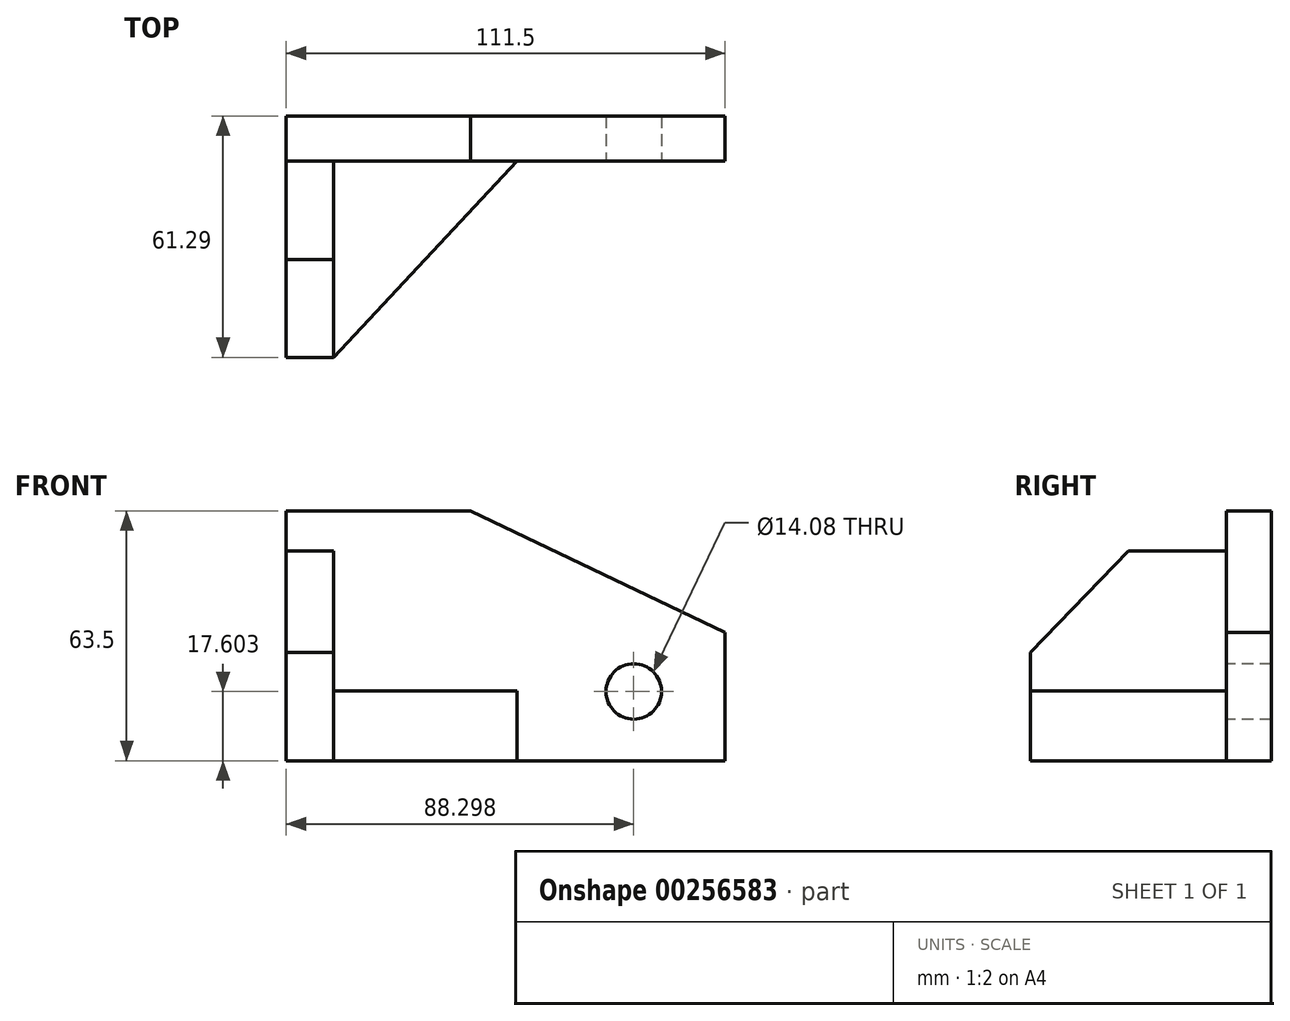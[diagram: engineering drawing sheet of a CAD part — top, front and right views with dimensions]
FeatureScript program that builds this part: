
annotation { "Feature Type Name" : "Feature", "Feature Type Description" : "" }
export const myFeature = defineFeature(function(context is Context, id is Id, definition is map)
    precondition{}
    {
        {
            var Q0;
            Q0=qCreatedBy(makeId("Top.planeOp"),FACE);
            var sketch = newSketch(context, id + "F0", { "sketchPlane" : qUnion([Q0])});
            skLineSegment(sketch, "E0.bottom", {"start": v(-51.05, 9.49) * mm, "end": v(60.45, 9.49) * mm});
            skLineSegment(sketch, "E0.top", {"start": v(-51.05, -51.8) * mm, "end": v(60.45, -51.8) * mm});
            skLineSegment(sketch, "E0.left", {"start": v(-51.05, 9.49) * mm, "end": v(-51.05, -51.8) * mm});
            skLineSegment(sketch, "E0.right", {"start": v(60.45, 9.49) * mm, "end": v(60.45, -51.8) * mm});
            skSolve(sketch);
        }
        {
            var Q0;
            Q0=makeQuery(id+"F0.imprint","IMPRINT",FACE,{"disambiguationData":[TD([[makeQuery(id+"F0.imprint","IMPRINT",EDGE,{"derivedFrom":sQuery(id+"F0.wireOp",EDGE,"E0.bottom")}),-1.0]])]});
            extrude(context, id + "F1", {"entities" : qUnion([Q0]), "depth" : 17.78 * mm});
        }
        {
            var Q0;
            Q0=makeQuery(id+"F1.opExtrude","CAP_FACE",FACE,{"disambiguationData":[OSD([sQuery(id+"F0.wireOp",EDGE,"E0.bottom"),sQuery(id+"F0.wireOp",EDGE,"E0.top"),sQuery(id+"F0.wireOp",EDGE,"E0.left"),sQuery(id+"F0.wireOp",EDGE,"E0.right")])],"isStart":false});
            var sketch = newSketch(context, id + "F2", { "sketchPlane" : qUnion([Q0])});
            skLineSegment(sketch, "E1.bottom", {"start": v(-51.05, 9.49) * mm, "end": v(60.45, 9.49) * mm});
            skLineSegment(sketch, "E1.top", {"start": v(-51.05, -1.98) * mm, "end": v(60.45, -1.98) * mm});
            skLineSegment(sketch, "E1.left", {"start": v(-51.05, 9.49) * mm, "end": v(-51.05, -1.98) * mm});
            skLineSegment(sketch, "E1.right", {"start": v(60.45, 9.49) * mm, "end": v(60.45, -1.98) * mm});
            skSolve(sketch);
        }
        {
            var Q0;
            Q0=makeQuery(id+"F2.imprint","IMPRINT",FACE,{"disambiguationData":[TD([[makeQuery(id+"F2.imprint","IMPRINT",EDGE,{"derivedFrom":sQuery(id+"F2.wireOp",EDGE,"E1.bottom")}),-1.0]])]});
            extrude(context, id + "F3", {"entities" : qUnion([Q0]), "operationType" : NewBodyOperationType.ADD, "depth" : 45.72 * mm});
        }
        {
            var Q0;
            Q0=makeQuery(id+"F1.opExtrude","CAP_FACE",FACE,{"disambiguationData":[OSD([sQuery(id+"F0.wireOp",EDGE,"E0.bottom"),sQuery(id+"F0.wireOp",EDGE,"E0.top"),sQuery(id+"F0.wireOp",EDGE,"E0.left"),sQuery(id+"F0.wireOp",EDGE,"E0.right")])],"isStart":false});
            var sketch = newSketch(context, id + "F4", { "sketchPlane" : qUnion([Q0])});
            skLineSegment(sketch, "E2.bottom", {"start": v(-51.05, -1.98) * mm, "end": v(-39.07, -1.98) * mm});
            skLineSegment(sketch, "E2.top", {"start": v(-51.05, -51.8) * mm, "end": v(-39.07, -51.8) * mm});
            skLineSegment(sketch, "E2.left", {"start": v(-51.05, -1.98) * mm, "end": v(-51.05, -51.8) * mm});
            skLineSegment(sketch, "E2.right", {"start": v(-39.07, -1.98) * mm, "end": v(-39.07, -51.8) * mm});
            skSolve(sketch);
        }
        {
            var Q0;
            Q0=makeQuery(id+"F4.imprint","IMPRINT",FACE,{"disambiguationData":[TD([[makeQuery(id+"F4.imprint","IMPRINT",EDGE,{"derivedFrom":sQuery(id+"F4.wireOp",EDGE,"E2.bottom")}),-1.0]])]});
            extrude(context, id + "F5", {"entities" : qUnion([Q0]), "operationType" : NewBodyOperationType.ADD, "depth" : 35.56 * mm});
        }
        {
            var Q0;
            Q0=makeQuery(id+"F5.opExtrude","SWEPT_FACE",FACE,{"disambiguationData":[OSD([sQuery(id+"F4.wireOp",EDGE,"E2.right")])]});
            var sketch = newSketch(context, id + "F6", { "sketchPlane" : qUnion([Q0])});
            skLineSegment(sketch, "E3", {"start": v(-26.89, 53.34) * mm, "end": v(-51.8, 27.57) * mm});
            skSolve(sketch);
        }
        {
            var Q0;
            {var subQ0=sQuery(id+"F6.wireOp",EDGE,"E3");Q0=makeQuery(id+"F6.imprint","IMPRINT",FACE,{"disambiguationData":[TD([[makeQuery(id+"F6.imprint","IMPRINT",EDGE,{"derivedFrom":subQ0}),-1.0]])]});}
            extrude(context, id + "F7", {"entities" : qUnion([Q0]), "operationType" : NewBodyOperationType.REMOVE, "oppositeDirection" : true, "depth" : 25.4 * mm});
        }
        {
            var Q0;
            Q0=makeQuery(id+"F3.opExtrude","SWEPT_FACE",FACE,{"disambiguationData":[OSD([sQuery(id+"F2.wireOp",EDGE,"E1.top")])]});
            var sketch = newSketch(context, id + "F8", { "sketchPlane" : qUnion([Q0])});
            skLineSegment(sketch, "E4", {"start": v(-4.2, 63.5) * mm, "end": v(60.45, 32.55) * mm});
            skSolve(sketch);
        }
        {
            var Q0;
            {var subQ0=sQuery(id+"F8.wireOp",EDGE,"E4");Q0=makeQuery(id+"F8.imprint","IMPRINT",FACE,{"disambiguationData":[TD([[makeQuery(id+"F8.imprint","IMPRINT",EDGE,{"derivedFrom":subQ0}),1.0]])]});}
            extrude(context, id + "F9", {"entities" : qUnion([Q0]), "operationType" : NewBodyOperationType.REMOVE, "oppositeDirection" : true, "depth" : 25.4 * mm});
        }
        {
            var Q0;
            Q0=makeQuery(id+"F1.opExtrude","CAP_FACE",FACE,{"disambiguationData":[OSD([sQuery(id+"F0.wireOp",EDGE,"E0.bottom"),sQuery(id+"F0.wireOp",EDGE,"E0.top"),sQuery(id+"F0.wireOp",EDGE,"E0.left"),sQuery(id+"F0.wireOp",EDGE,"E0.right")])],"isStart":false});
            var sketch = newSketch(context, id + "F10", { "sketchPlane" : qUnion([Q0])});
            skLineSegment(sketch, "E5", {"start": v(7.54, -1.98) * mm, "end": v(-39.07, -51.8) * mm});
            skSolve(sketch);
        }
        {
            var Q0;
            {var subQ0=sQuery(id+"F10.wireOp",EDGE,"E5");Q0=makeQuery(id+"F10.imprint","IMPRINT",FACE,{"disambiguationData":[TD([[makeQuery(id+"F10.imprint","IMPRINT",EDGE,{"derivedFrom":subQ0}),1.0]])]});}
            extrude(context, id + "F11", {"entities" : qUnion([Q0]), "operationType" : NewBodyOperationType.REMOVE, "oppositeDirection" : true, "depth" : 25.4 * mm});
        }
        {
            var Q0;
            {var subQ0=sQuery(id+"F2.wireOp",EDGE,"E1.top");Q0=makeQuery(id+"F11.boolean.opBoolean","MERGE",FACE,{"derivedFrom":[makeQuery(id+"F3.opExtrude","SWEPT_FACE",FACE,{"disambiguationData":[OSD([subQ0])]}),makeQuery(id+"F11.opExtrude","SWEPT_FACE",FACE,{"disambiguationData":[OSD([subQ0])]})]});}
            var sketch = newSketch(context, id + "F12", { "sketchPlane" : qUnion([Q0])});
            skLineSegment(sketch, "E6", {"start": v(37.25, 17.6) * mm, "end": v(37.25, 38.24) * mm});
            skLineSegment(sketch, "E7", {"start": v(37.25, 17.6) * mm, "end": v(19.46, 17.6) * mm});
            skLineSegment(sketch, "E8", {"start": v(37.25, 17.6) * mm, "end": v(37.25, 3.02) * mm});
            skLineSegment(sketch, "E9", {"start": v(37.25, 17.6) * mm, "end": v(55.22, 17.6) * mm});
            skCircle(sketch, "E10", {"center": v(37.25, 17.6) * mm, "radius": 7.04 * mm});
            skSolve(sketch);
        }
        {
            var Q0;
            {var subQ1=sQuery(id+"F12.wireOp",EDGE,"E6");var subQ3=sQuery(id+"F12.wireOp",EDGE,"E10");var subQ4=makeQuery(id+"F12.imprint","INTERSECT",VERTEX,{"derivedFrom":[subQ1,subQ3]});Q0=makeQuery(id+"F12.imprint","IMPRINT",FACE,{"disambiguationData":[TD([[makeQuery(id+"F12.imprint","IMPRINT",EDGE,{"disambiguationData":[TD([[subQ4,-1.0]])],"derivedFrom":subQ3}),1.0]])]});}
            var Q1;
            {var subQ1=sQuery(id+"F12.wireOp",EDGE,"E6");var subQ3=sQuery(id+"F12.wireOp",EDGE,"E10");var subQ4=makeQuery(id+"F12.imprint","INTERSECT",VERTEX,{"derivedFrom":[subQ1,subQ3]});Q1=makeQuery(id+"F12.imprint","IMPRINT",FACE,{"disambiguationData":[TD([[makeQuery(id+"F12.imprint","IMPRINT",EDGE,{"disambiguationData":[TD([[subQ4,1.0]])],"derivedFrom":subQ3}),1.0]])]});}
            var Q2;
            {var subQ1=sQuery(id+"F12.wireOp",EDGE,"E7");var subQ3=sQuery(id+"F12.wireOp",EDGE,"E10");var subQ4=makeQuery(id+"F12.imprint","INTERSECT",VERTEX,{"derivedFrom":[subQ1,subQ3]});Q2=makeQuery(id+"F12.imprint","IMPRINT",FACE,{"disambiguationData":[TD([[makeQuery(id+"F12.imprint","IMPRINT",EDGE,{"disambiguationData":[TD([[subQ4,-1.0]])],"derivedFrom":subQ3}),1.0]])]});}
            var Q3;
            {var subQ1=sQuery(id+"F12.wireOp",EDGE,"E8");var subQ3=sQuery(id+"F12.wireOp",EDGE,"E10");var subQ4=makeQuery(id+"F12.imprint","INTERSECT",VERTEX,{"derivedFrom":[subQ1,subQ3]});Q3=makeQuery(id+"F12.imprint","IMPRINT",FACE,{"disambiguationData":[TD([[makeQuery(id+"F12.imprint","IMPRINT",EDGE,{"disambiguationData":[TD([[subQ4,-1.0]])],"derivedFrom":subQ3}),1.0]])]});}
            extrude(context, id + "F13", {"entities" : qUnion([Q0, Q1, Q2, Q3]), "operationType" : NewBodyOperationType.REMOVE, "oppositeDirection" : true, "depth" : 25.4 * mm});
        }
    });
